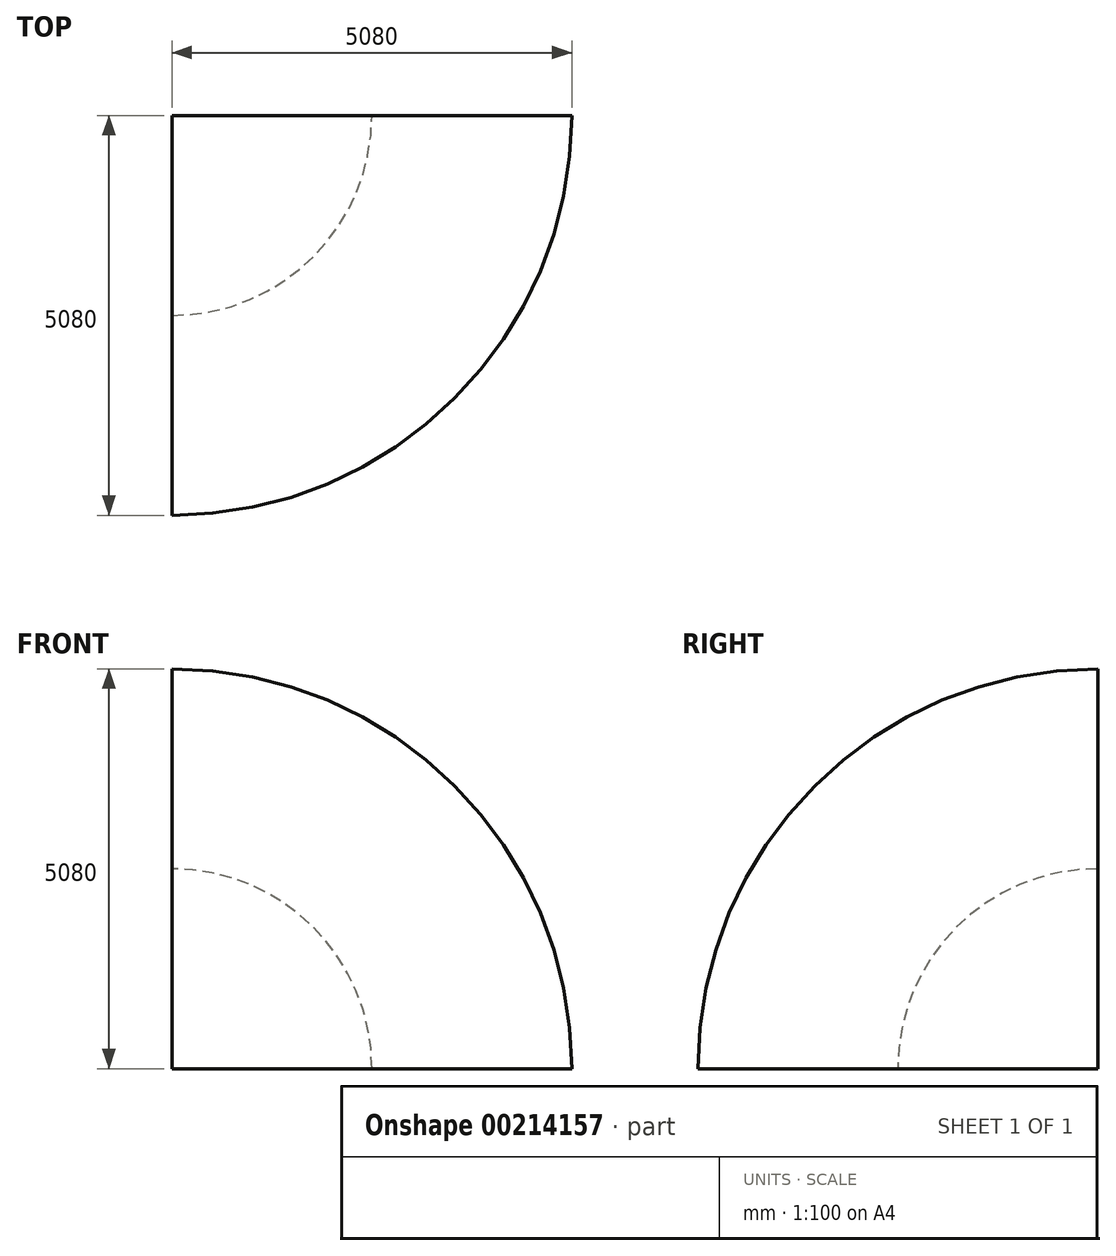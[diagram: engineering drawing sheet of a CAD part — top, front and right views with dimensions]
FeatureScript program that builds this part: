
annotation { "Feature Type Name" : "Feature", "Feature Type Description" : "" }
export const myFeature = defineFeature(function(context is Context, id is Id, definition is map)
    precondition{}
    {
        {
            var Q0;
            Q0=qCreatedBy(makeId("Front.planeOp"),FACE);
            var sketch = newSketch(context, id + "F0", { "sketchPlane" : qUnion([Q0])});
            skLineSegment(sketch, "E0", {"start": v(0, 2540) * mm, "end": v(0, 5080) * mm});
            skArc(sketch, "E1", {"start": v(5080, 0) * mm, "mid": v(3592.1, 3592.1) * mm, "end": v(0, 5080) * mm});
            skLineSegment(sketch, "E2", {"start": v(2540, 0) * mm, "end": v(5080, 0) * mm});
            skArc(sketch, "E3", {"start": v(2540, 0) * mm, "mid": v(1796.05, 1796.05) * mm, "end": v(0, 2540) * mm});
            skSolve(sketch);
        }
        {
            var Q0;
            Q0=qCreatedBy(makeId("Front.planeOp"),FACE);
            var sketch = newSketch(context, id + "F1", { "sketchPlane" : qUnion([Q0])});
            skLineSegment(sketch, "E4", {"start": v(0, 5891.7) * mm, "end": v(0, 0) * mm});
            skSolve(sketch);
        }
        {
            var Q0;
            Q0=makeQuery(id+"F0.imprint","IMPRINT",FACE,{"disambiguationData":[TD([[makeQuery(id+"F0.imprint","IMPRINT",EDGE,{"derivedFrom":sQuery(id+"F0.wireOp",EDGE,"E0")}),-1.0]])]});
            var Q1;
            Q1=sQuery(id+"F1.wireOp",EDGE,"E4");
            revolve(context, id + "F2", {"entities" : qUnion([Q0]), "axis" : qUnion([Q1]), "revolveType" : RevolveType.ONE_DIRECTION, "angle" : 90 * degree});
        }
    });
